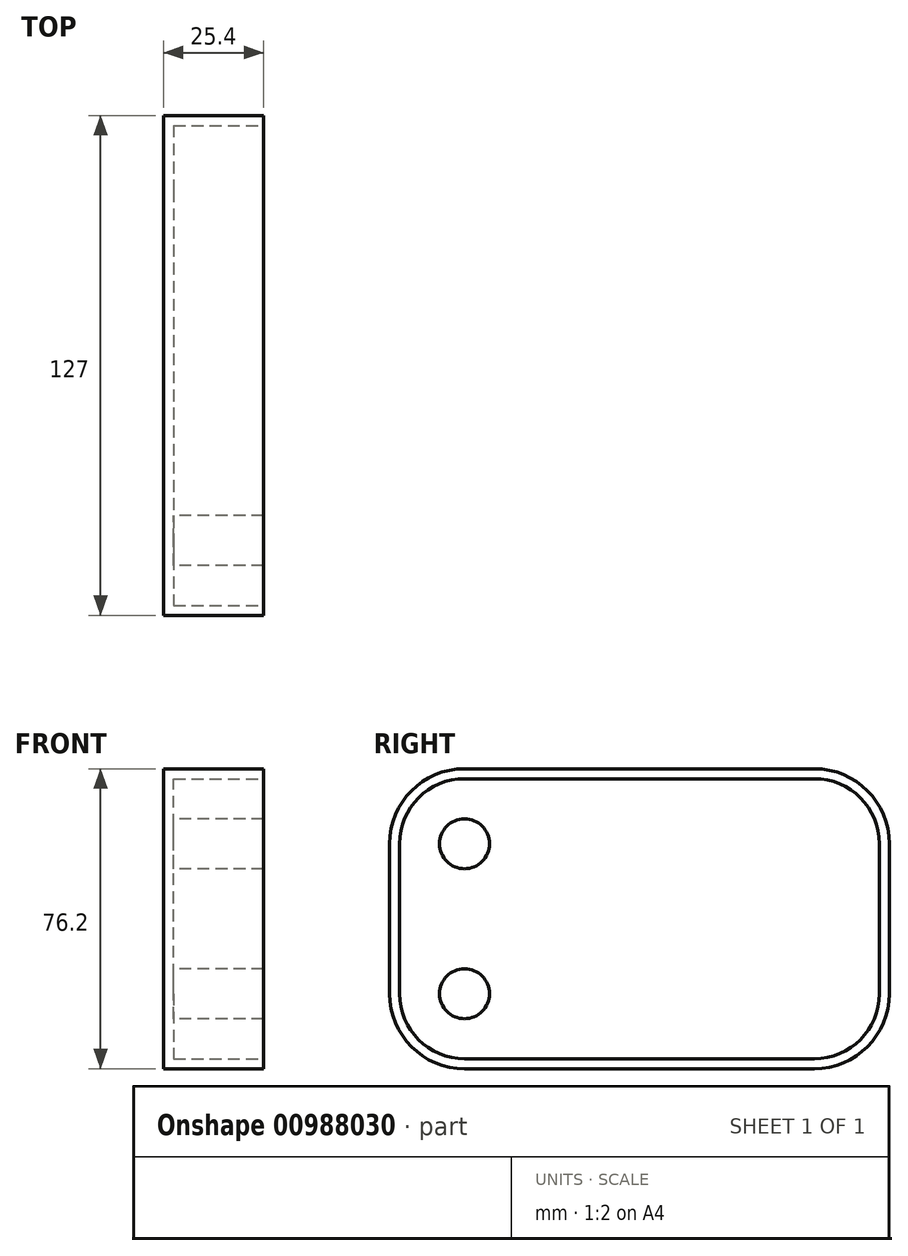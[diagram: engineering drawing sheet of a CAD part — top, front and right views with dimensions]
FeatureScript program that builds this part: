
annotation { "Feature Type Name" : "Feature", "Feature Type Description" : "" }
export const myFeature = defineFeature(function(context is Context, id is Id, definition is map)
    precondition{}
    {
        {
            var Q0;
            Q0=qCreatedBy(makeId("Right.planeOp"),FACE);
            var sketch = newSketch(context, id + "F0", { "sketchPlane" : qUnion([Q0])});
            skLineSegment(sketch, "E0.bottom", {"start": v(0, 0) * mm, "end": v(-127, 0) * mm});
            skLineSegment(sketch, "E0.top", {"start": v(0, 76.2) * mm, "end": v(-127, 76.2) * mm});
            skLineSegment(sketch, "E0.left", {"start": v(0, 0) * mm, "end": v(0, 76.2) * mm});
            skLineSegment(sketch, "E0.right", {"start": v(-127, 0) * mm, "end": v(-127, 76.2) * mm});
            skSolve(sketch);
        }
        {
            var Q0;
            Q0=makeQuery(id+"F0.imprint","IMPRINT",FACE,{"disambiguationData":[TD([[makeQuery(id+"F0.imprint","IMPRINT",EDGE,{"derivedFrom":sQuery(id+"F0.wireOp",EDGE,"E0.bottom")}),-1.0]])]});
            extrude(context, id + "F1", {"entities" : qUnion([Q0]), "oppositeDirection" : true, "depth" : 25.4 * mm, "offsetDistance" : 25.4 * mm});
        }
        {
            var Q0;
            Q0=makeQuery(id+"F1.opExtrude","SWEPT_EDGE",EDGE,{"disambiguationData":[OSD([sQuery(id+"F0.wireOp",EDGE,"E0.top"),sQuery(id+"F0.wireOp",EDGE,"E0.right")])]});
            var Q1;
            Q1=makeQuery(id+"F1.opExtrude","SWEPT_EDGE",EDGE,{"disambiguationData":[OSD([sQuery(id+"F0.wireOp",EDGE,"E0.bottom"),sQuery(id+"F0.wireOp",EDGE,"E0.right")])]});
            var Q2;
            Q2=makeQuery(id+"F1.opExtrude","SWEPT_EDGE",EDGE,{"disambiguationData":[OSD([sQuery(id+"F0.wireOp",EDGE,"E0.top"),sQuery(id+"F0.wireOp",EDGE,"E0.left")])]});
            var Q3;
            Q3=makeQuery(id+"F1.opExtrude","SWEPT_EDGE",EDGE,{"disambiguationData":[OSD([sQuery(id+"F0.wireOp",EDGE,"E0.bottom"),sQuery(id+"F0.wireOp",EDGE,"E0.left")])]});
            fillet(context, id + "F2", {"entities" : qUnion([Q0, Q1, Q2, Q3]), "radius" : 19.05 * mm, "tangentPropagation" : true, "allowEdgeOverflow" : false});
        }
        {
            var Q0;
            Q0=makeQuery(id+"F1.opExtrude","CAP_FACE",FACE,{"disambiguationData":[OSD([sQuery(id+"F0.wireOp",EDGE,"E0.bottom"),sQuery(id+"F0.wireOp",EDGE,"E0.top"),sQuery(id+"F0.wireOp",EDGE,"E0.left"),sQuery(id+"F0.wireOp",EDGE,"E0.right")])],"isStart":true});
            shell(context, id + "F3", {"entities" : qUnion([Q0]), "thickness" : 2.54 * mm});
        }
        {
            var Q0;
            Q0=makeQuery(id+"F3.opShell","OFFSET_FACE",FACE,{"disambiguationData":[OSD([sQuery(id+"F0.wireOp",EDGE,"E0.bottom"),sQuery(id+"F0.wireOp",EDGE,"E0.top"),sQuery(id+"F0.wireOp",EDGE,"E0.left"),sQuery(id+"F0.wireOp",EDGE,"E0.right")])]});
            var sketch = newSketch(context, id + "F4", { "sketchPlane" : qUnion([Q0])});
            skArc(sketch, "E1.0", {"start": v(-107.95, 73.66) * mm, "mid": v(-119.62, 68.82) * mm, "end": v(-124.46, 57.15) * mm});
            skArc(sketch, "E2.0", {"start": v(-124.46, 19.05) * mm, "mid": v(-119.62, 7.38) * mm, "end": v(-107.95, 2.54) * mm});
            skArc(sketch, "E3.0", {"start": v(-19.05, 2.54) * mm, "mid": v(-7.38, 7.38) * mm, "end": v(-2.54, 19.05) * mm});
            skArc(sketch, "E4.0", {"start": v(-2.54, 57.15) * mm, "mid": v(-7.38, 68.82) * mm, "end": v(-19.05, 73.66) * mm});
            skCircle(sketch, "E5", {"center": v(-107.95, 57.15) * mm, "radius": 6.35 * mm});
            skCircle(sketch, "E6", {"center": v(-107.95, 19.05) * mm, "radius": 6.35 * mm});
            skSolve(sketch);
        }
        {
            var Q0;
            Q0=makeQuery(id+"F4.imprint","IMPRINT",FACE,{"disambiguationData":[TD([[makeQuery(id+"F4.imprint","IMPRINT",EDGE,{"derivedFrom":sQuery(id+"F4.wireOp",EDGE,"E5")}),1.0]])]});
            var Q1;
            Q1=makeQuery(id+"F4.imprint","IMPRINT",FACE,{"disambiguationData":[TD([[makeQuery(id+"F4.imprint","IMPRINT",EDGE,{"derivedFrom":sQuery(id+"F4.wireOp",EDGE,"E6")}),1.0]])]});
            var Q2;
            Q2=makeQuery(id+"F1.opExtrude","CAP_FACE",FACE,{"disambiguationData":[OSD([sQuery(id+"F0.wireOp",EDGE,"E0.bottom"),sQuery(id+"F0.wireOp",EDGE,"E0.top"),sQuery(id+"F0.wireOp",EDGE,"E0.left"),sQuery(id+"F0.wireOp",EDGE,"E0.right")])],"isStart":true});
            extrude(context, id + "F5", {"entities" : qUnion([Q0, Q1]), "operationType" : NewBodyOperationType.ADD, "endBound" : BoundingType.UP_TO_SURFACE, "depth" : 25.4 * mm, "endBoundEntityFace" : qUnion([Q2]), "offsetDistance" : 25.4 * mm});
        }
    });
